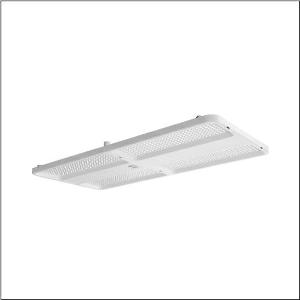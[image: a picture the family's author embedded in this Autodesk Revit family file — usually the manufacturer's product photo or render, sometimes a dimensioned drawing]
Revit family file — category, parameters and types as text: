
# Revit family: highbay_21_maxi_52hn12db4mda01
name_source: partatom
category: Lighting Fixtures
units: mm (PartAtom-declared; Revit-internal decimal feet)

## family parameters
Cut with Voids When Loaded = No
Host = Face
Light Source = No
Part Type = Normal
Room Calculation Point = No
Round Connector Dimension = Use Diameter
Shared = No

## types (1)
- --- (1 x LED, 28000 lm, 144.5 W, 4000K)
    Apparent Load = 144 VA
    CIE Flux Codes = 90 98 100 100 100
    Color Rendering = 80
    Color Temperature = 4000K
    Default Elevation = 1800 mm
    Description = high bay luminaire Highbay 21 maxi; direct symmetric wide distribution, light control with lens of PMMA; UGR ≤ 22 (X = 4H | Y = 8H | S = 0.25H | reflection values 70/50/20); luminous flux: 28.000lm; light colour: 840, colour temperature: 4000K, MacAdam ≤ 3 SDCM (initial), colour rendering: CRI > 80; luminous efficacy: 193,8lm/W; rated service life: 75.000h (L80) at AT= ta max; control: Bluetooth Mesh; for wireless networking: Node multi-sensor luminaire for setting up a local control solution without a higher-level application controller, intelligence completely integrated into the luminaire; with auto-swarm function: leading lighting creates safety. The function is already active without any „out-of-the-box“ commissioning; commissioning is not necessary thanks to „out-of-the-box“ functions: basic functions (presence lighting, follow-up times, fading times, etc.) are already preset at the factory; no control line such as DALI between the Node multi-sensor luminaires and Nodes is required, wireless integration of other Node luminaires and Node multi-sensor luminaires into the network is possible; number of Node multi-sensor luminaires in the project can be expanded as required, network sizes > 300 Nodes can be realized; can also be connected to lighting or building automation via various gateways upon request; integrated DALI2 ECG provides luminaire data (according to IEC62386, Part 251), energy data (Part 252), and monitoring and analytics data (Part 253) to higher-level systems for further processing; luminaire with PIR sensor (passive-infrared); with light sensor; luminaire connection: terminal, 5-pole, max. 2.5mm² (cable entry for one cable, Ø 8.5..16mm); mains connection: 230..240V, AC 50/60Hz; connected load: 144,5W; protection rating (complete): IP65; insulation class (complete): insulation class I (protective earthing); protection symbol: D; certification: CE, UKCA; internal wiring halogen-free; luminaire LABS conformity tested according to VDMA 24364:2018-05; Suitable for use in the food industry according to the specifications of IFS-Food, HACCP and/or BRC; housing frame of high-performance plastic PA6, matt traffic white (RAL 9016); cover of PMMA; dimension (LxWxH): 946 x 442 x 72mm; permissible operating ambient temperature: -20..+45°C (reducing of maximum allowable ambient temperature of 5°C with ceiling mounting); packaging unit: 1 piece; (delivery without accessories; please order mounting accessories separately)
    Height = 72 mm  [stored 0.23622 ft]
    Lamp = 1 x LED
    Lamp Light Flux = 28000 lm
    Lamp Power = 144.5 W
    Lamp count = 1
    Length = 946 mm
    Luminous efficacy = 194 lm/W
    Manufacturer = Siteco
    ModVariant = No
    Model = 52HN12DB4MDA01
    Mounting Place = Ceiling
    Mounting Type = Pendant
    Number of Poles = 1
    OnlyDefault = Yes
    Power Factor = 1
    Product Name = Highbay 21 maxi
    Product group = high bay luminaire
    ProductGroupID = 902
    Protection Class = Protection class I
    Protection Degree = IP 65
    RLX_Detail_Level = 1
    RLX_Emergency_Light_Flux = 0 lm
    RLX_Emergency_Type = 0
    RLX_Emergency_Type_DB = No
    RlxData = <blob elided: 128965 chars, md5=3d827102>
    Socket = socket
    Standby Power = 0 W
    System Light Flux = 28000 lm
    System Power = 144 W
    Type Comments = factory setting: luminous flux: 100 % | dim-lin: 254 | 668 mA
    Type Image = l_1363267.jpg
    URL = http://relux.com
    VarID = @adj_014297
    Voltage = 0 V
    Weight = 0.00 kg
    Width = 442 mm

note: [stored X ft] marks values corroborated as IEEE doubles in the binary element streams (Revit-internal decimal feet)

## geometry (parser evidence)
native form markers: Blend x4, Sweep x11
no freeform markers — native parametric forms only
